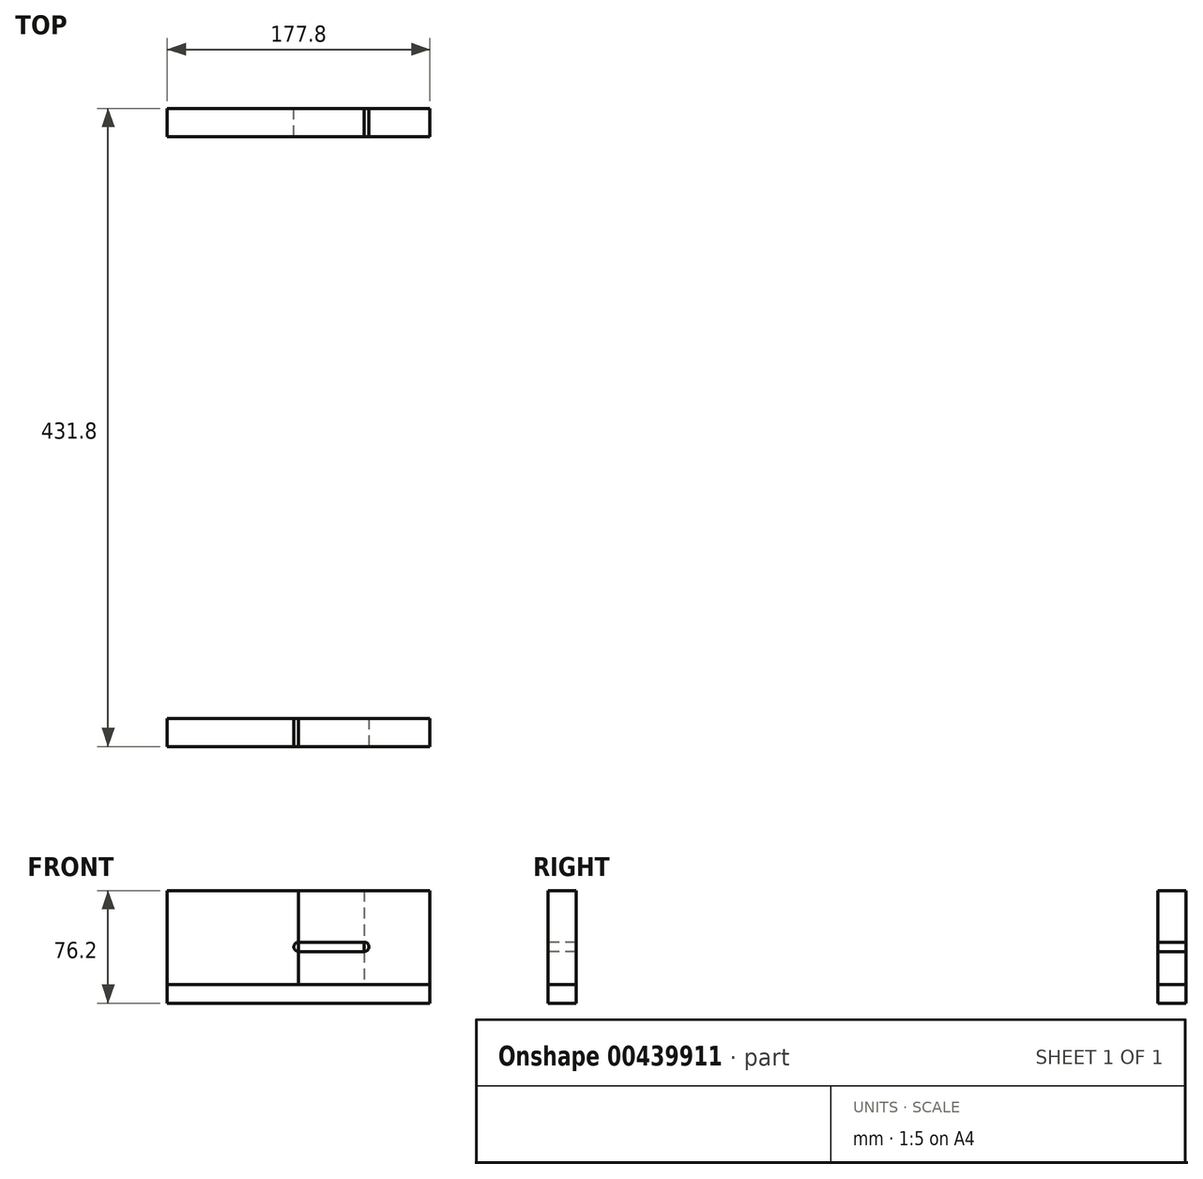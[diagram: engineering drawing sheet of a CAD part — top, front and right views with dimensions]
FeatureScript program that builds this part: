
annotation { "Feature Type Name" : "Feature", "Feature Type Description" : "" }
export const myFeature = defineFeature(function(context is Context, id is Id, definition is map)
    precondition{}
    {
        {
            var Q0;
            Q0=qCreatedBy(makeId("Top.planeOp"),FACE);
            var sketch = newSketch(context, id + "F0", { "sketchPlane" : qUnion([Q0])});
            skLineSegment(sketch, "E0", {"start": v(0, 0) * mm, "end": v(0, 215.9) * mm});
            skLineSegment(sketch, "E1.MirrorCS", {"start": v(0, 0) * mm, "end": v(0, -215.9) * mm});
            skLineSegment(sketch, "E2", {"start": v(0, 215.9) * mm, "end": v(-177.8, 215.9) * mm});
            skLineSegment(sketch, "E3", {"start": v(-177.8, 215.9) * mm, "end": v(-177.8, -215.9) * mm});
            skLineSegment(sketch, "E4", {"start": v(-177.8, -215.9) * mm, "end": v(0, -215.9) * mm});
            skLineSegment(sketch, "E5", {"start": v(-177.8, -215.9) * mm, "end": v(-177.8, -196.85) * mm});
            skLineSegment(sketch, "E6", {"start": v(-177.8, -196.85) * mm, "end": v(0, -196.85) * mm});
            skLineSegment(sketch, "E7", {"start": v(0, -196.85) * mm, "end": v(0, -215.9) * mm});
            skLineSegment(sketch, "E8.MirrorCS", {"start": v(-177.8, 196.85) * mm, "end": v(0, 196.85) * mm});
            skSolve(sketch);
        }
        {
            var Q0;
            Q0=makeQuery(id+"F0.imprint","IMPRINT",FACE,{"disambiguationData":[TD([[makeQuery(id+"F0.imprint","IMPRINT",EDGE,{"derivedFrom":sQuery(id+"F0.wireOp",EDGE,"E4")}),1.0]])]});
            var Q1;
            {var subQ1=sQuery(id+"F0.wireOp",EDGE,"E1.MirrorCS");Q1=makeQuery(id+"F0.imprint","IMPRINT",FACE,{"disambiguationData":[TD([[makeQuery(id+"F0.imprint","IMPRINT",EDGE,{"derivedFrom":subQ1}),-1.0]])]});}
            var Q2;
            {var subQ0=sQuery(id+"F0.wireOp",EDGE,"E2");Q2=makeQuery(id+"F0.imprint","IMPRINT",FACE,{"disambiguationData":[TD([[makeQuery(id+"F0.imprint","IMPRINT",EDGE,{"derivedFrom":subQ0}),1.0]])]});}
            extrude(context, id + "F1", {"entities" : qUnion([Q0, Q1, Q2]), "oppositeDirection" : true, "depth" : 12.7 * mm});
        }
        {
            var Q0;
            {var subQ0=sQuery(id+"F0.wireOp",EDGE,"E2");Q0=makeQuery(id+"F0.imprint","IMPRINT",FACE,{"disambiguationData":[TD([[makeQuery(id+"F0.imprint","IMPRINT",EDGE,{"derivedFrom":subQ0}),1.0]])]});}
            extrude(context, id + "F2", {"entities" : qUnion([Q0]), "depth" : 63.5 * mm});
        }
        {
            var Q0;
            Q0=makeQuery(id+"F0.imprint","IMPRINT",FACE,{"disambiguationData":[TD([[makeQuery(id+"F0.imprint","IMPRINT",EDGE,{"derivedFrom":sQuery(id+"F0.wireOp",EDGE,"E4")}),1.0]])]});
            extrude(context, id + "F3", {"entities" : qUnion([Q0]), "depth" : 63.5 * mm});
        }
        {
            var Q0;
            Q0=makeQuery(id+"F3.opExtrude","SWEPT_FACE",FACE,{"disambiguationData":[OSD([sQuery(id+"F0.wireOp",EDGE,"E4")])]});
            var sketch = newSketch(context, id + "F4", { "sketchPlane" : qUnion([Q0])});
            skLineSegment(sketch, "E9", {"start": v(-177.8, 63.5) * mm, "end": v(-88.9, 63.5) * mm});
            skLineSegment(sketch, "E10", {"start": v(-88.9, 63.5) * mm, "end": v(-88.9, 0) * mm});
            skLineSegment(sketch, "E11", {"start": v(-88.9, 0) * mm, "end": v(-88.9, 25.4) * mm});
            skCircle(sketch, "E12", {"center": v(-88.9, 25.4) * mm, "radius": 3.18 * mm});
            skLineSegment(sketch, "E13", {"start": v(-88.9, 0) * mm, "end": v(-44.45, 0) * mm});
            skLineSegment(sketch, "E14", {"start": v(-44.45, 0) * mm, "end": v(-44.45, 63.5) * mm});
            skCircle(sketch, "E15", {"center": v(-44.45, 25.4) * mm, "radius": 3.18 * mm});
            skLineSegment(sketch, "E16", {"start": v(-44.45, 28.58) * mm, "end": v(-88.9, 28.58) * mm});
            skLineSegment(sketch, "E17", {"start": v(-88.9, 22.23) * mm, "end": v(-44.45, 22.23) * mm});
            skSolve(sketch);
        }
        {
            var Q0;
            {var subQ0=sQuery(id+"F4.wireOp",EDGE,"E11");var subQ1=sQuery(id+"F4.wireOp",EDGE,"E10");var subQ2=makeQuery(id+"F4.imprint","INTERSECT",VERTEX,{"derivedFrom":[subQ1,subQ0]});Q0=makeQuery(id+"F4.imprint","IMPRINT",FACE,{"disambiguationData":[TD([[makeQuery(id+"F4.imprint","IMPRINT",EDGE,{"disambiguationData":[TD([[subQ2,1.0]])],"derivedFrom":subQ1}),1.0]])]});}
            var Q1;
            {var subQ0=sQuery(id+"F4.wireOp",EDGE,"E15");var subQ1=sQuery(id+"F4.wireOp",EDGE,"E14");var subQ2=makeQuery(id+"F4.imprint","INTERSECT",VERTEX,{"derivedFrom":[subQ1,subQ0,sQuery(id+"F4.wireOp",EDGE,"E16")]});Q1=makeQuery(id+"F4.imprint","IMPRINT",FACE,{"disambiguationData":[TD([[makeQuery(id+"F4.imprint","IMPRINT",EDGE,{"disambiguationData":[TD([[subQ2,1.0]])],"derivedFrom":subQ1}),1.0]])]});}
            var Q2;
            {var subQ0=sQuery(id+"F4.wireOp",EDGE,"E15");var subQ1=sQuery(id+"F4.wireOp",EDGE,"E14");var subQ2=makeQuery(id+"F4.imprint","INTERSECT",VERTEX,{"derivedFrom":[subQ1,subQ0,sQuery(id+"F4.wireOp",EDGE,"E16")]});Q2=makeQuery(id+"F4.imprint","IMPRINT",FACE,{"disambiguationData":[TD([[makeQuery(id+"F4.imprint","IMPRINT",EDGE,{"disambiguationData":[TD([[subQ2,1.0]])],"derivedFrom":subQ1}),-1.0]])]});}
            var Q3;
            {var subQ0=sQuery(id+"F4.wireOp",EDGE,"E11");var subQ1=sQuery(id+"F4.wireOp",EDGE,"E10");var subQ2=makeQuery(id+"F4.imprint","INTERSECT",VERTEX,{"derivedFrom":[subQ1,subQ0]});Q3=makeQuery(id+"F4.imprint","IMPRINT",FACE,{"disambiguationData":[TD([[makeQuery(id+"F4.imprint","IMPRINT",EDGE,{"disambiguationData":[TD([[subQ2,1.0]])],"derivedFrom":subQ1}),-1.0]])]});}
            var Q4;
            {var subQ0=sQuery(id+"F4.wireOp",EDGE,"E16");Q4=makeQuery(id+"F4.imprint","IMPRINT",FACE,{"disambiguationData":[TD([[makeQuery(id+"F4.imprint","IMPRINT",EDGE,{"derivedFrom":subQ0}),1.0]])]});}
            extrude(context, id + "F5", {"entities" : qUnion([Q0, Q1, Q2, Q3, Q4]), "operationType" : NewBodyOperationType.REMOVE, "oppositeDirection" : true, "depth" : 25.4 * mm});
        }
        {
            var Q0;
            Q0=makeQuery(id+"F2.opExtrude","SWEPT_FACE",FACE,{"disambiguationData":[OSD([sQuery(id+"F0.wireOp",EDGE,"E2")])]});
            var sketch = newSketch(context, id + "F6", { "sketchPlane" : qUnion([Q0])});
            skLineSegment(sketch, "E18", {"start": v(0, 63.5) * mm, "end": v(44.45, 63.5) * mm});
            skLineSegment(sketch, "E19", {"start": v(44.45, 63.5) * mm, "end": v(44.45, 0) * mm});
            skLineSegment(sketch, "E20", {"start": v(44.45, 0) * mm, "end": v(88.9, 0) * mm});
            skLineSegment(sketch, "E21", {"start": v(88.9, 0) * mm, "end": v(88.9, 63.5) * mm});
            skLineSegment(sketch, "E22", {"start": v(44.45, 0) * mm, "end": v(44.45, 25.4) * mm});
            skCircle(sketch, "E23", {"center": v(44.45, 25.4) * mm, "radius": 3.18 * mm});
            skCircle(sketch, "E24", {"center": v(88.9, 25.4) * mm, "radius": 3.18 * mm});
            skLineSegment(sketch, "E25", {"start": v(44.45, 28.58) * mm, "end": v(88.9, 28.58) * mm});
            skLineSegment(sketch, "E26", {"start": v(44.45, 22.23) * mm, "end": v(88.9, 22.23) * mm});
            skSolve(sketch);
        }
        {
            var Q0;
            {var subQ0=sQuery(id+"F6.wireOp",EDGE,"E25");Q0=makeQuery(id+"F6.imprint","IMPRINT",FACE,{"disambiguationData":[TD([[makeQuery(id+"F6.imprint","IMPRINT",EDGE,{"derivedFrom":subQ0}),-1.0]])]});}
            var Q1;
            {var subQ0=sQuery(id+"F6.wireOp",EDGE,"E22");var subQ1=sQuery(id+"F6.wireOp",EDGE,"E19");var subQ2=makeQuery(id+"F6.imprint","INTERSECT",VERTEX,{"derivedFrom":[subQ1,subQ0]});Q1=makeQuery(id+"F6.imprint","IMPRINT",FACE,{"disambiguationData":[TD([[makeQuery(id+"F6.imprint","IMPRINT",EDGE,{"disambiguationData":[TD([[subQ2,1.0]])],"derivedFrom":subQ1}),1.0]])]});}
            var Q2;
            {var subQ0=sQuery(id+"F6.wireOp",EDGE,"E22");var subQ1=sQuery(id+"F6.wireOp",EDGE,"E19");var subQ2=makeQuery(id+"F6.imprint","INTERSECT",VERTEX,{"derivedFrom":[subQ1,subQ0]});Q2=makeQuery(id+"F6.imprint","IMPRINT",FACE,{"disambiguationData":[TD([[makeQuery(id+"F6.imprint","IMPRINT",EDGE,{"disambiguationData":[TD([[subQ2,1.0]])],"derivedFrom":subQ1}),-1.0]])]});}
            var Q3;
            {var subQ0=sQuery(id+"F6.wireOp",EDGE,"E24");var subQ1=sQuery(id+"F6.wireOp",EDGE,"E21");var subQ2=makeQuery(id+"F6.imprint","INTERSECT",VERTEX,{"derivedFrom":[subQ1,subQ0,sQuery(id+"F6.wireOp",EDGE,"E25")]});Q3=makeQuery(id+"F6.imprint","IMPRINT",FACE,{"disambiguationData":[TD([[makeQuery(id+"F6.imprint","IMPRINT",EDGE,{"disambiguationData":[TD([[subQ2,1.0]])],"derivedFrom":subQ1}),1.0]])]});}
            var Q4;
            {var subQ0=sQuery(id+"F6.wireOp",EDGE,"E24");var subQ1=sQuery(id+"F6.wireOp",EDGE,"E21");var subQ2=makeQuery(id+"F6.imprint","INTERSECT",VERTEX,{"derivedFrom":[subQ1,subQ0,sQuery(id+"F6.wireOp",EDGE,"E25")]});Q4=makeQuery(id+"F6.imprint","IMPRINT",FACE,{"disambiguationData":[TD([[makeQuery(id+"F6.imprint","IMPRINT",EDGE,{"disambiguationData":[TD([[subQ2,1.0]])],"derivedFrom":subQ1}),-1.0]])]});}
            extrude(context, id + "F7", {"entities" : qUnion([Q0, Q1, Q2, Q3, Q4]), "operationType" : NewBodyOperationType.REMOVE, "oppositeDirection" : true, "depth" : 25.4 * mm});
        }
    });
